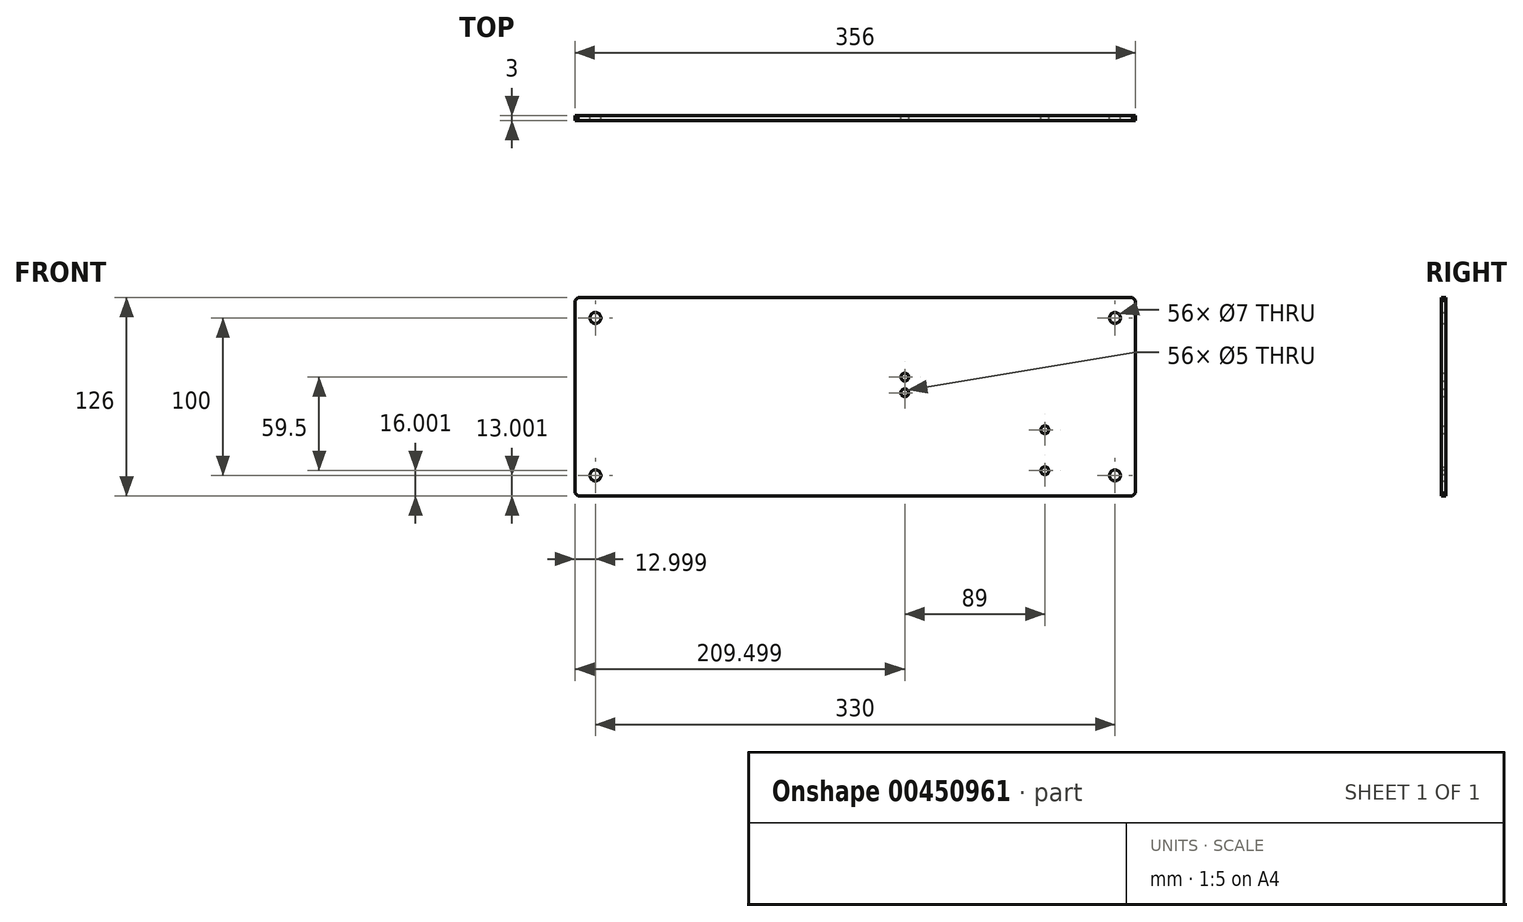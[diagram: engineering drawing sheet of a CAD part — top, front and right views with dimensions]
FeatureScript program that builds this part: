
annotation { "Feature Type Name" : "Feature", "Feature Type Description" : "" }
export const myFeature = defineFeature(function(context is Context, id is Id, definition is map)
    precondition{}
    {
        {
            var Q0;
            Q0=qCreatedBy(makeId("Front.planeOp"),FACE);
            var sketch = newSketch(context, id + "F0", { "sketchPlane" : qUnion([Q0])});
            skLineSegment(sketch, "E0", {"start": v(-144.63, -252.42) * mm, "end": v(-496.63, -252.42) * mm});
            skLineSegment(sketch, "E1", {"start": v(-142.63, -250.42) * mm, "end": v(-144.63, -252.42) * mm});
            skLineSegment(sketch, "E2", {"start": v(-498.63, -250.42) * mm, "end": v(-496.63, -252.42) * mm});
            skLineSegment(sketch, "E3", {"start": v(-498.63, -128.42) * mm, "end": v(-498.63, -250.42) * mm});
            skLineSegment(sketch, "E4", {"start": v(-142.63, -128.42) * mm, "end": v(-142.63, -250.42) * mm});
            skLineSegment(sketch, "E5", {"start": v(-496.63, -126.42) * mm, "end": v(-498.63, -128.42) * mm});
            skLineSegment(sketch, "E6", {"start": v(-496.63, -126.42) * mm, "end": v(-144.63, -126.42) * mm});
            skLineSegment(sketch, "E7", {"start": v(-142.63, -128.42) * mm, "end": v(-144.63, -126.42) * mm});
            skLineSegment(sketch, "E8", {"start": v(-200.13, -240.17) * mm, "end": v(-200.13, -232.67) * mm});
            skCircle(sketch, "E9", {"center": v(-200.13, -236.42) * mm, "radius": 2.07 * mm});
            skCircle(sketch, "E10", {"center": v(-200.13, -236.42) * mm, "radius": 2.5 * mm});
            skLineSegment(sketch, "E11", {"start": v(-196.38, -236.42) * mm, "end": v(-203.88, -236.42) * mm});
            skLineSegment(sketch, "E12", {"start": v(-200.13, -214.17) * mm, "end": v(-200.13, -206.67) * mm});
            skCircle(sketch, "E13", {"center": v(-200.13, -210.42) * mm, "radius": 2.07 * mm});
            skCircle(sketch, "E14", {"center": v(-200.13, -210.42) * mm, "radius": 2.5 * mm});
            skLineSegment(sketch, "E15", {"start": v(-196.38, -210.42) * mm, "end": v(-203.88, -210.42) * mm});
            skLineSegment(sketch, "E16", {"start": v(-289.13, -190.67) * mm, "end": v(-289.13, -183.17) * mm});
            skCircle(sketch, "E17", {"center": v(-289.13, -186.92) * mm, "radius": 2.07 * mm});
            skCircle(sketch, "E18", {"center": v(-289.13, -186.92) * mm, "radius": 2.5 * mm});
            skLineSegment(sketch, "E19", {"start": v(-285.38, -186.92) * mm, "end": v(-292.88, -186.92) * mm});
            skLineSegment(sketch, "E20", {"start": v(-289.13, -180.67) * mm, "end": v(-289.13, -173.17) * mm});
            skCircle(sketch, "E21", {"center": v(-289.13, -176.92) * mm, "radius": 2.07 * mm});
            skCircle(sketch, "E22", {"center": v(-289.13, -176.92) * mm, "radius": 2.5 * mm});
            skLineSegment(sketch, "E23", {"start": v(-285.38, -176.92) * mm, "end": v(-292.88, -176.92) * mm});
            skLineSegment(sketch, "E24", {"start": v(-40.37, -126.42) * mm, "end": v(-43.37, -126.42) * mm});
            skLineSegment(sketch, "E25", {"start": v(-43.37, -126.42) * mm, "end": v(-43.37, -252.42) * mm});
            skLineSegment(sketch, "E26", {"start": v(-40.37, -126.42) * mm, "end": v(-40.37, -252.42) * mm});
            skLineSegment(sketch, "E27", {"start": v(-40.37, -252.42) * mm, "end": v(-43.37, -252.42) * mm});
            skCircle(sketch, "E28", {"center": v(-155.63, -139.42) * mm, "radius": 3.5 * mm});
            skLineSegment(sketch, "E29", {"start": v(-155.63, -143.97) * mm, "end": v(-155.63, -134.87) * mm});
            skLineSegment(sketch, "E30", {"start": v(-151.08, -139.42) * mm, "end": v(-160.18, -139.42) * mm});
            skCircle(sketch, "E31", {"center": v(-155.63, -239.42) * mm, "radius": 3.5 * mm});
            skCircle(sketch, "E32", {"center": v(-485.63, -239.42) * mm, "radius": 3.5 * mm});
            skCircle(sketch, "E33", {"center": v(-485.63, -139.42) * mm, "radius": 3.5 * mm});
            skLineSegment(sketch, "E34", {"start": v(-160.18, -239.42) * mm, "end": v(-151.08, -239.42) * mm});
            skLineSegment(sketch, "E35", {"start": v(-155.63, -243.97) * mm, "end": v(-155.63, -234.87) * mm});
            skLineSegment(sketch, "E36", {"start": v(-481.08, -239.42) * mm, "end": v(-490.18, -239.42) * mm});
            skLineSegment(sketch, "E37", {"start": v(-485.63, -234.87) * mm, "end": v(-485.63, -243.97) * mm});
            skLineSegment(sketch, "E38", {"start": v(-481.08, -139.42) * mm, "end": v(-490.18, -139.42) * mm});
            skLineSegment(sketch, "E39", {"start": v(-485.63, -134.87) * mm, "end": v(-485.63, -143.97) * mm});
            skSolve(sketch);
        }
        {
            var Q0;
            Q0=makeQuery(id+"F0.imprint","IMPRINT",FACE,{"disambiguationData":[TD([[makeQuery(id+"F0.imprint","IMPRINT",EDGE,{"derivedFrom":sQuery(id+"F0.wireOp",EDGE,"E0")}),-1.0]])]});
            extrude(context, id + "F1", {"entities" : qUnion([Q0]), "depth" : 3 * mm});
        }
    });
